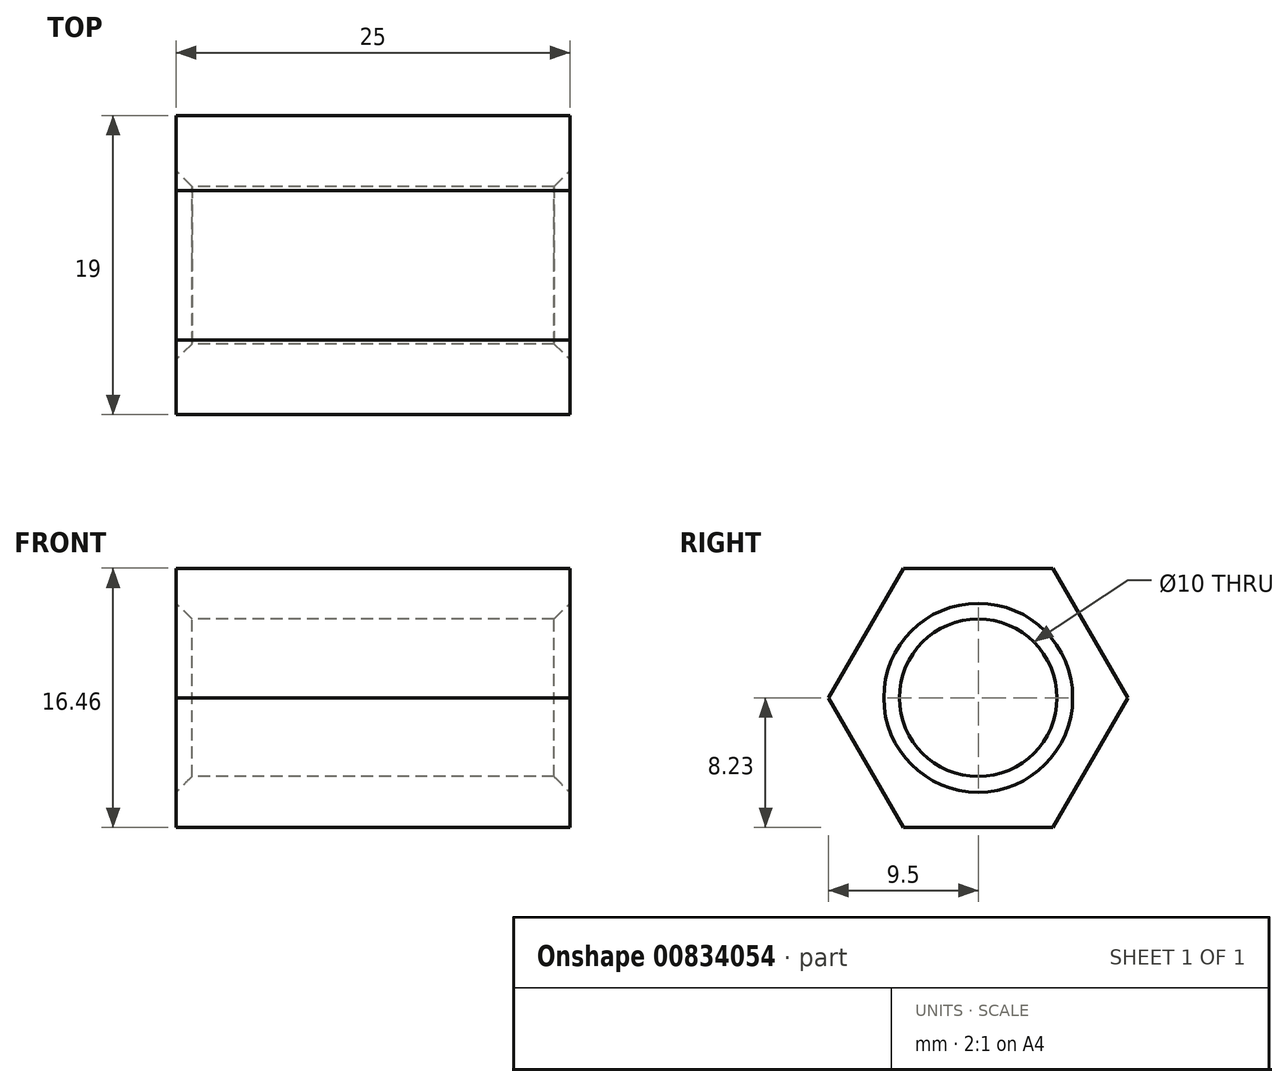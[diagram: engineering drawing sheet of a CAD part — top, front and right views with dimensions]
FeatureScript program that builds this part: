
annotation { "Feature Type Name" : "Feature", "Feature Type Description" : "" }
export const myFeature = defineFeature(function(context is Context, id is Id, definition is map)
    precondition{}
    {
        {
            var Q0;
            Q0=qCreatedBy(makeId("Right.planeOp"),FACE);
            var sketch = newSketch(context, id + "F0", { "sketchPlane" : qUnion([Q0])});
            skCircle(sketch, "E0", {"center": v(0, 0) * mm, "radius": 9.5 * mm, "construction": true});
            skLineSegment(sketch, "E1", {"start": v(-4.75, 8.23) * mm, "end": v(4.75, 8.23) * mm});
            skLineSegment(sketch, "E2", {"start": v(4.75, 8.23) * mm, "end": v(9.5, 0) * mm});
            skLineSegment(sketch, "E3", {"start": v(9.5, 0) * mm, "end": v(4.75, -8.23) * mm});
            skLineSegment(sketch, "E4", {"start": v(4.75, -8.23) * mm, "end": v(-4.75, -8.23) * mm});
            skLineSegment(sketch, "E5", {"start": v(-4.75, -8.23) * mm, "end": v(-9.5, 0) * mm});
            skLineSegment(sketch, "E6", {"start": v(-9.5, 0) * mm, "end": v(-4.75, 8.23) * mm});
            skCircle(sketch, "E7", {"center": v(0, 0) * mm, "radius": 5 * mm});
            skSolve(sketch);
        }
        {
            var Q0;
            Q0=makeQuery(id+"F0.imprint","IMPRINT",FACE,{"disambiguationData":[TD([[makeQuery(id+"F0.imprint","IMPRINT",EDGE,{"derivedFrom":sQuery(id+"F0.wireOp",EDGE,"E1")}),-1.0]])]});
            extrude(context, id + "F1", {"entities" : qUnion([Q0]), "depth" : 25 * mm, "offsetDistance" : 25 * mm});
        }
        {
            var Q0;
            Q0=makeQuery(id+"F1.opExtrude","CAP_EDGE",EDGE,{"disambiguationData":[OSD([sQuery(id+"F0.wireOp",EDGE,"E7")])],"isStart":true});
            var Q1;
            Q1=makeQuery(id+"F1.opExtrude","CAP_EDGE",EDGE,{"disambiguationData":[OSD([sQuery(id+"F0.wireOp",EDGE,"E7")])],"isStart":false});
            chamfer(context, id + "F2", {"entities" : qUnion([Q0, Q1]), "width" : 1 * mm, "tangentPropagation" : true});
        }
    });
